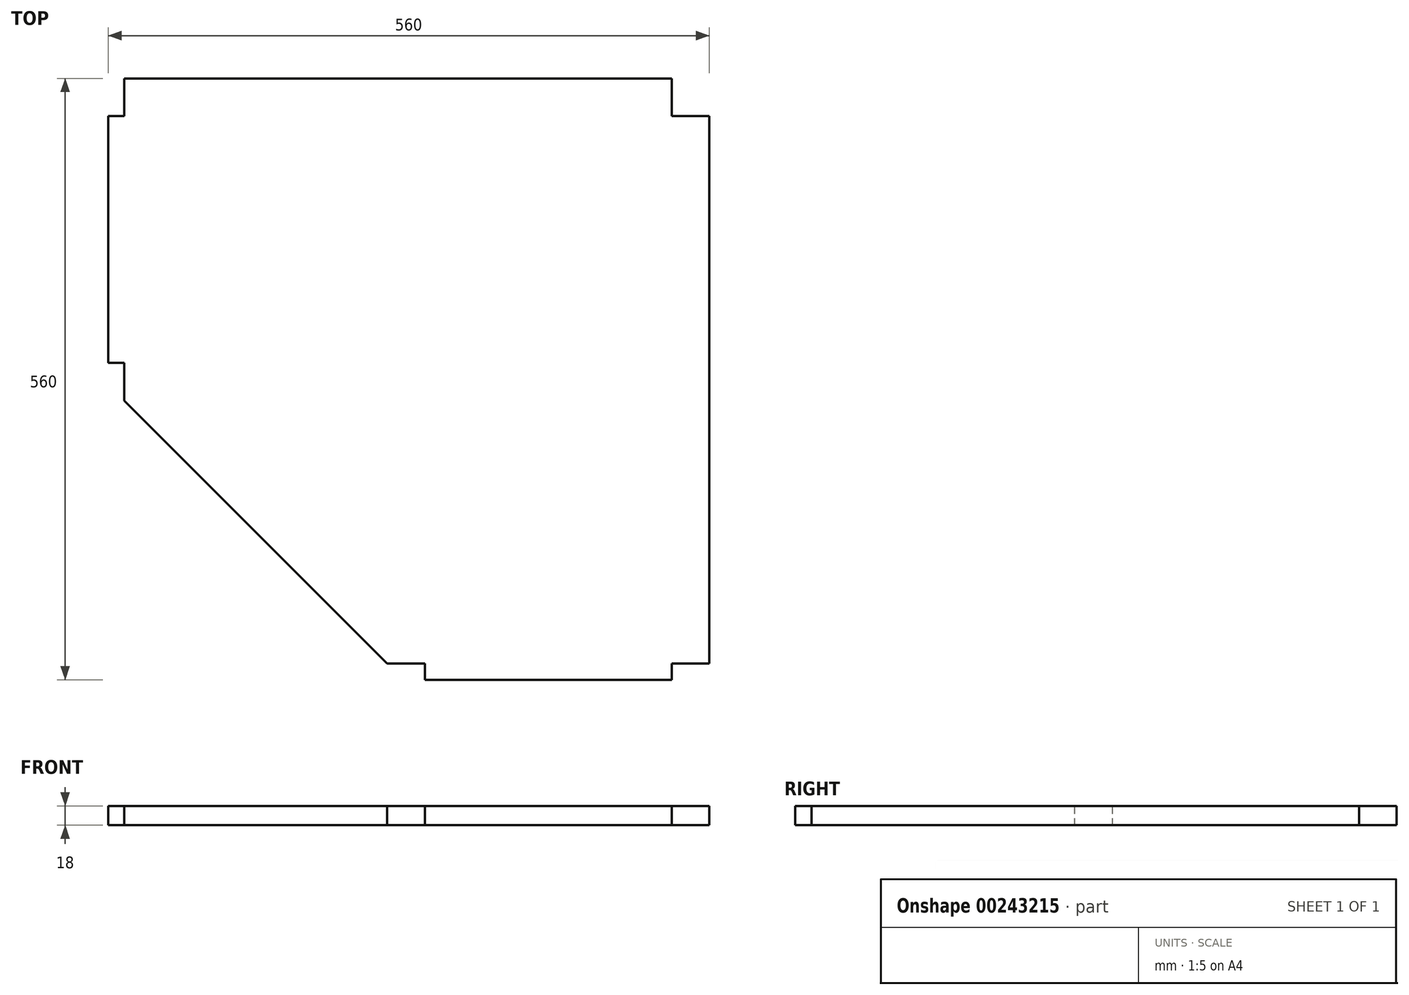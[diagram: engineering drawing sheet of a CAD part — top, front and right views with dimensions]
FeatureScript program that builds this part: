
annotation { "Feature Type Name" : "Feature", "Feature Type Description" : "" }
export const myFeature = defineFeature(function(context is Context, id is Id, definition is map)
    precondition{}
    {
        {
            assignVariable(context, id + "F0", {"variableType" : VariableType.LENGTH, "name" : "ShelfThickness", "lengthValue" : 18 * mm});
        }
        {
            var Q0;
            Q0=qCreatedBy(makeId("Top.planeOp"),FACE);
            var sketch = newSketch(context, id + "F1", { "sketchPlane" : qUnion([Q0])});
            skLineSegment(sketch, "E0", {"start": v(15, 0) * mm, "end": v(15, 35) * mm});
            skLineSegment(sketch, "E1", {"start": v(15, 35) * mm, "end": v(0, 35) * mm});
            skLineSegment(sketch, "E2", {"start": v(0, 35) * mm, "end": v(0, 150) * mm});
            skLineSegment(sketch, "E3", {"start": v(0, 150) * mm, "end": v(210, 150) * mm});
            skLineSegment(sketch, "E4", {"start": v(210, 150) * mm, "end": v(210, 0) * mm});
            skLineSegment(sketch, "E5", {"start": v(210, 0) * mm, "end": v(15, 0) * mm});
            skSolve(sketch);
        }
        {
            var Q0;
            Q0 = qSketchRegion(id + "F1", true);
            extrude(context, id + "F2", {"entities" : qUnion([Q0]), "depth" : getVariable(context, 'ShelfThickness'), "offsetDistance" : 25 * mm});
        }
        {
            var Q0;
            Q0=makeQuery(id+"F2.opExtrude","SWEPT_FACE",FACE,{"disambiguationData":[OSD([sQuery(id+"F1.wireOp",EDGE,"E1")])]});
            var sketch = newSketch(context, id + "F3", { "sketchPlane" : qUnion([Q0])});
            skArc(sketch, "E6", {"start": v(9, 4.25) * mm, "mid": v(5.25, 8) * mm, "end": v(1.5, 4.25) * mm});
            skLineSegment(sketch, "E7", {"start": v(1.5, 4.25) * mm, "end": v(1.5, 0) * mm});
            skLineSegment(sketch, "E8", {"start": v(1.5, 0) * mm, "end": v(9, 0) * mm});
            skLineSegment(sketch, "E9", {"start": v(9, 0) * mm, "end": v(9, 4.25) * mm});
            skCircle(sketch, "E10", {"center": v(5.28, 5) * mm, "radius": 3 * mm, "construction": true});
            skSolve(sketch);
        }
        {
            var Q0;
            Q0 = qSketchRegion(id + "F3", true);
            extrude(context, id + "F4", {"entities" : qUnion([Q0]), "operationType" : NewBodyOperationType.REMOVE, "oppositeDirection" : true, "depth" : 20 * mm, "offsetDistance" : 25 * mm});
        }
        {
            var Q0;
            Q0=makeQuery(id+"F2.opExtrude","SWEPT_BODY",BODY,{"disambiguationData":[OSD([sQuery(id+"F1.wireOp",EDGE,"E0"),sQuery(id+"F1.wireOp",EDGE,"E1"),sQuery(id+"F1.wireOp",EDGE,"E2"),sQuery(id+"F1.wireOp",EDGE,"E3"),sQuery(id+"F1.wireOp",EDGE,"E4"),sQuery(id+"F1.wireOp",EDGE,"E5")])]});
            var Q1;
            Q1=makeQuery(id+"F2.opExtrude","SWEPT_FACE",FACE,{"disambiguationData":[OSD([sQuery(id+"F1.wireOp",EDGE,"E3")])]});
            mirror(context, id + "F5", {"operationType" : NewBodyOperationType.ADD, "entities" : qUnion([Q0]), "mirrorPlane" : qUnion([Q1])});
        }
        {
            var Q0;
            Q0=makeQuery(id+"F2.opExtrude","SWEPT_BODY",BODY,{"disambiguationData":[OSD([sQuery(id+"F1.wireOp",EDGE,"E0"),sQuery(id+"F1.wireOp",EDGE,"E1"),sQuery(id+"F1.wireOp",EDGE,"E2"),sQuery(id+"F1.wireOp",EDGE,"E3"),sQuery(id+"F1.wireOp",EDGE,"E4"),sQuery(id+"F1.wireOp",EDGE,"E5")])]});
            var Q1;
            {var subQ0=makeQuery(id+"F2.opExtrude","SWEPT_FACE",FACE,{"disambiguationData":[OSD([sQuery(id+"F1.wireOp",EDGE,"E4")])]});Q1=makeQuery(id+"F5.boolean.opBoolean","MERGE",FACE,{"derivedFrom":[subQ0,makeQuery(id+"F5.opPattern","COPY",FACE,{"derivedFrom":subQ0,"instanceName":"1"})]});}
            mirror(context, id + "F6", {"operationType" : NewBodyOperationType.ADD, "entities" : qUnion([Q0]), "mirrorPlane" : qUnion([Q1])});
        }
        {
            var Q0;
            Q0=qCreatedBy(makeId("Top.planeOp"),FACE);
            var sketch = newSketch(context, id + "F7", { "sketchPlane" : qUnion([Q0])});
            skLineSegment(sketch, "E11", {"start": v(15, 0) * mm, "end": v(15, 35) * mm});
            skLineSegment(sketch, "E12", {"start": v(15, 35) * mm, "end": v(0, 35) * mm});
            skLineSegment(sketch, "E13", {"start": v(0, 35) * mm, "end": v(0, 265) * mm});
            skLineSegment(sketch, "E14", {"start": v(0, 265) * mm, "end": v(15, 265) * mm});
            skLineSegment(sketch, "E15", {"start": v(15, 265) * mm, "end": v(15, 300) * mm});
            skLineSegment(sketch, "E16", {"start": v(15, 300) * mm, "end": v(525, 300) * mm});
            skLineSegment(sketch, "E17", {"start": v(525, 300) * mm, "end": v(525, 265) * mm});
            skLineSegment(sketch, "E18", {"start": v(525, 265) * mm, "end": v(137.5, -122.5) * mm});
            skLineSegment(sketch, "E19", {"start": v(137.5, -122.5) * mm, "end": v(15, 0) * mm});
            skSolve(sketch);
        }
        {
            var Q0;
            Q0=makeQuery(id+"F7.imprint","IMPRINT",FACE,{"disambiguationData":[TD([[makeQuery(id+"F7.imprint","IMPRINT",EDGE,{"derivedFrom":sQuery(id+"F7.wireOp",EDGE,"E11")}),-1.0]])]});
            extrude(context, id + "F8", {"entities" : qUnion([Q0]), "depth" : getVariable(context, 'ShelfThickness'), "offsetDistance" : 25 * mm});
        }
        {
            var Q0;
            Q0=makeQuery(id+"F8.opExtrude","SWEPT_BODY",BODY,{"disambiguationData":[OSD([sQuery(id+"F7.wireOp",EDGE,"E11"),sQuery(id+"F7.wireOp",EDGE,"E12"),sQuery(id+"F7.wireOp",EDGE,"E13"),sQuery(id+"F7.wireOp",EDGE,"E14"),sQuery(id+"F7.wireOp",EDGE,"E15"),sQuery(id+"F7.wireOp",EDGE,"E16"),sQuery(id+"F7.wireOp",EDGE,"E17"),sQuery(id+"F7.wireOp",EDGE,"E18"),sQuery(id+"F7.wireOp",EDGE,"E19")])]});
            var Q1;
            Q1=makeQuery(id+"F8.opExtrude","SWEPT_FACE",FACE,{"disambiguationData":[OSD([sQuery(id+"F7.wireOp",EDGE,"E18")])]});
            mirror(context, id + "F9", {"operationType" : NewBodyOperationType.ADD, "entities" : qUnion([Q0]), "mirrorPlane" : qUnion([Q1])});
        }
    });
